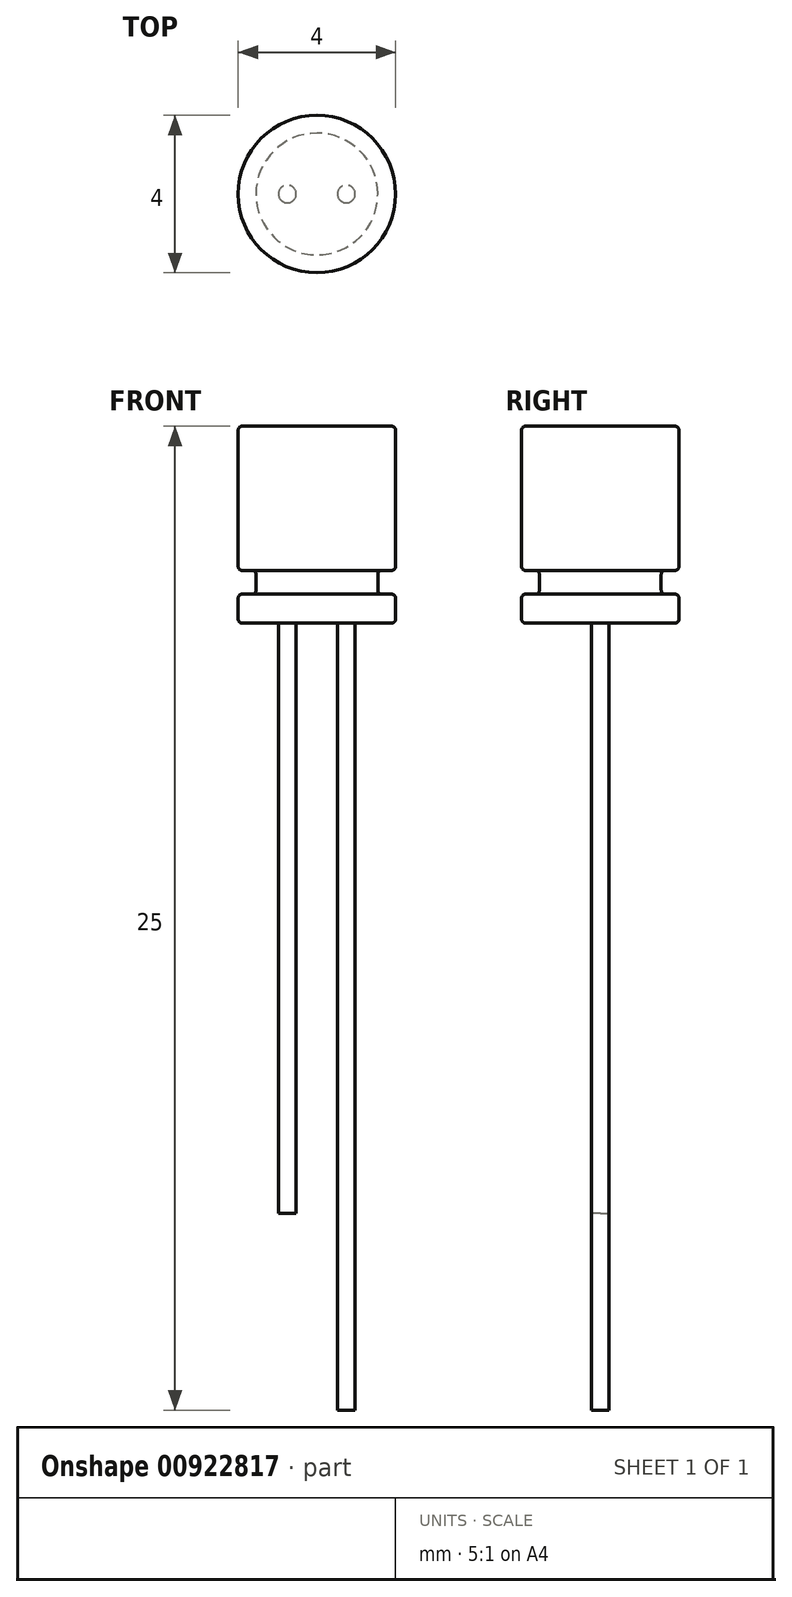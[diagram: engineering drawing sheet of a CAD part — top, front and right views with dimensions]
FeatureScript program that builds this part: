
annotation { "Feature Type Name" : "Feature", "Feature Type Description" : "" }
export const myFeature = defineFeature(function(context is Context, id is Id, definition is map)
    precondition{}
    {
        {
            var Q0;
            Q0=qCreatedBy(makeId("Top.planeOp"),FACE);
            var sketch = newSketch(context, id + "F0", { "sketchPlane" : qUnion([Q0])});
            skCircle(sketch, "E0", {"center": v(0, 0) * mm, "radius": 2 * mm});
            skSolve(sketch);
        }
        {
            var Q0;
            Q0=makeQuery(id+"F0.imprint","IMPRINT",FACE,{"disambiguationData":[TD([[makeQuery(id+"F0.imprint","IMPRINT",EDGE,{"derivedFrom":sQuery(id+"F0.wireOp",EDGE,"E0")}),1.0]])]});
            extrude(context, id + "F1", {"entities" : qUnion([Q0]), "depth" : 5 * mm, "offsetDistance" : 25 * mm});
        }
        {
            var Q0;
            Q0=qCreatedBy(makeId("Front.planeOp"),FACE);
            var sketch = newSketch(context, id + "F2", { "sketchPlane" : qUnion([Q0])});
            skLineSegment(sketch, "E1.bottom", {"start": v(1.55, 1.34) * mm, "end": v(2.6, 1.34) * mm});
            skLineSegment(sketch, "E1.top", {"start": v(1.55, 0.73) * mm, "end": v(2.6, 0.73) * mm});
            skLineSegment(sketch, "E1.left", {"start": v(1.55, 1.34) * mm, "end": v(1.55, 0.73) * mm});
            skLineSegment(sketch, "E1.right", {"start": v(2.6, 1.34) * mm, "end": v(2.6, 0.73) * mm});
            skSolve(sketch);
        }
        {
            var Q0;
            Q0=makeQuery(id+"F2.imprint","IMPRINT",FACE,{"disambiguationData":[TD([[makeQuery(id+"F2.imprint","IMPRINT",EDGE,{"derivedFrom":sQuery(id+"F2.wireOp",EDGE,"E1.bottom")}),-1.0]])]});
            var Q1;
            Q1=makeQuery(id+"F1.opExtrude","CAP_EDGE",EDGE,{"disambiguationData":[OSD([sQuery(id+"F0.wireOp",EDGE,"E0")])],"isStart":true});
            revolve(context, id + "F3", {"operationType" : NewBodyOperationType.REMOVE, "surfaceOperationType" : NewSurfaceOperationType.NEW, "entities" : qUnion([Q0]), "axis" : qUnion([Q1]), "revolveType" : RevolveType.FULL, "oppositeDirection" : true});
        }
        {
            var Q0;
            Q0=makeQuery(id+"F3.boolean.opBoolean","INTERSECT",EDGE,{"derivedFrom":[makeQuery(id+"F1.opExtrude","SWEPT_FACE",FACE,{"disambiguationData":[OSD([sQuery(id+"F0.wireOp",EDGE,"E0")])]}),makeQuery(id+"F3.opRevolve","SWEPT_FACE",FACE,{"disambiguationData":[OSD([sQuery(id+"F2.wireOp",EDGE,"E1.bottom")])]})]});
            var Q1;
            Q1=makeQuery(id+"F3.boolean.opBoolean","COPY",EDGE,{"derivedFrom":makeQuery(id+"F3.opRevolve","SWEPT_EDGE",EDGE,{"disambiguationData":[OSD([sQuery(id+"F2.wireOp",EDGE,"E1.bottom"),sQuery(id+"F2.wireOp",EDGE,"E1.left")])]})});
            var Q2;
            Q2=makeQuery(id+"F3.boolean.opBoolean","COPY",EDGE,{"derivedFrom":makeQuery(id+"F3.opRevolve","SWEPT_EDGE",EDGE,{"disambiguationData":[OSD([sQuery(id+"F2.wireOp",EDGE,"E1.top"),sQuery(id+"F2.wireOp",EDGE,"E1.left")])]})});
            var Q3;
            Q3=makeQuery(id+"F3.boolean.opBoolean","INTERSECT",EDGE,{"derivedFrom":[makeQuery(id+"F1.opExtrude","SWEPT_FACE",FACE,{"disambiguationData":[OSD([sQuery(id+"F0.wireOp",EDGE,"E0")])]}),makeQuery(id+"F3.opRevolve","SWEPT_FACE",FACE,{"disambiguationData":[OSD([sQuery(id+"F2.wireOp",EDGE,"E1.top")])]})]});
            var Q4;
            Q4=makeQuery(id+"F1.opExtrude","CAP_EDGE",EDGE,{"disambiguationData":[OSD([sQuery(id+"F0.wireOp",EDGE,"E0")])],"isStart":false});
            var Q5;
            Q5=makeQuery(id+"F1.opExtrude","CAP_EDGE",EDGE,{"disambiguationData":[OSD([sQuery(id+"F0.wireOp",EDGE,"E0")])],"isStart":true});
            fillet(context, id + "F4", {"entities" : qUnion([Q0, Q1, Q2, Q3, Q4, Q5]), "radius" : 0.1 * mm, "tangentPropagation" : true, "allowEdgeOverflow" : false});
        }
        {
            var Q0;
            Q0=makeQuery(id+"F1.opExtrude","CAP_FACE",FACE,{"disambiguationData":[OSD([sQuery(id+"F0.wireOp",EDGE,"E0")])],"isStart":true});
            var sketch = newSketch(context, id + "F5", { "sketchPlane" : qUnion([Q0])});
            skLineSegment(sketch, "E2", {"start": v(0, 0) * mm, "end": v(0.75, 0) * mm});
            skLineSegment(sketch, "E3", {"start": v(0.75, 0) * mm, "end": v(-0.75, 0) * mm});
            skCircle(sketch, "E4", {"center": v(0.75, 0) * mm, "radius": 0.23 * mm});
            skCircle(sketch, "E5", {"center": v(-0.75, 0) * mm, "radius": 0.23 * mm});
            skSolve(sketch);
        }
        {
            var Q0;
            Q0=makeQuery(id+"F5.imprint","IMPRINT",FACE,{"disambiguationData":[TD([[makeQuery(id+"F5.imprint","IMPRINT",EDGE,{"derivedFrom":sQuery(id+"F5.wireOp",EDGE,"E5")}),1.0]])]});
            var Q1;
            Q1=makeQuery(id+"F5.imprint","IMPRINT",FACE,{"disambiguationData":[TD([[makeQuery(id+"F5.imprint","IMPRINT",EDGE,{"derivedFrom":sQuery(id+"F5.wireOp",EDGE,"E4")}),1.0]])]});
            extrude(context, id + "F6", {"entities" : qUnion([Q0, Q1]), "operationType" : NewBodyOperationType.ADD, "depth" : 15 * mm, "offsetDistance" : 25 * mm});
        }
        {
            var Q0;
            Q0=makeQuery(id+"F6.opExtrude","CAP_FACE",FACE,{"disambiguationData":[OSD([sQuery(id+"F5.wireOp",EDGE,"E4")])],"isStart":false});
            extrude(context, id + "F7", {"entities" : qUnion([Q0]), "operationType" : NewBodyOperationType.ADD, "depth" : 5 * mm, "offsetDistance" : 25 * mm});
        }
    });
